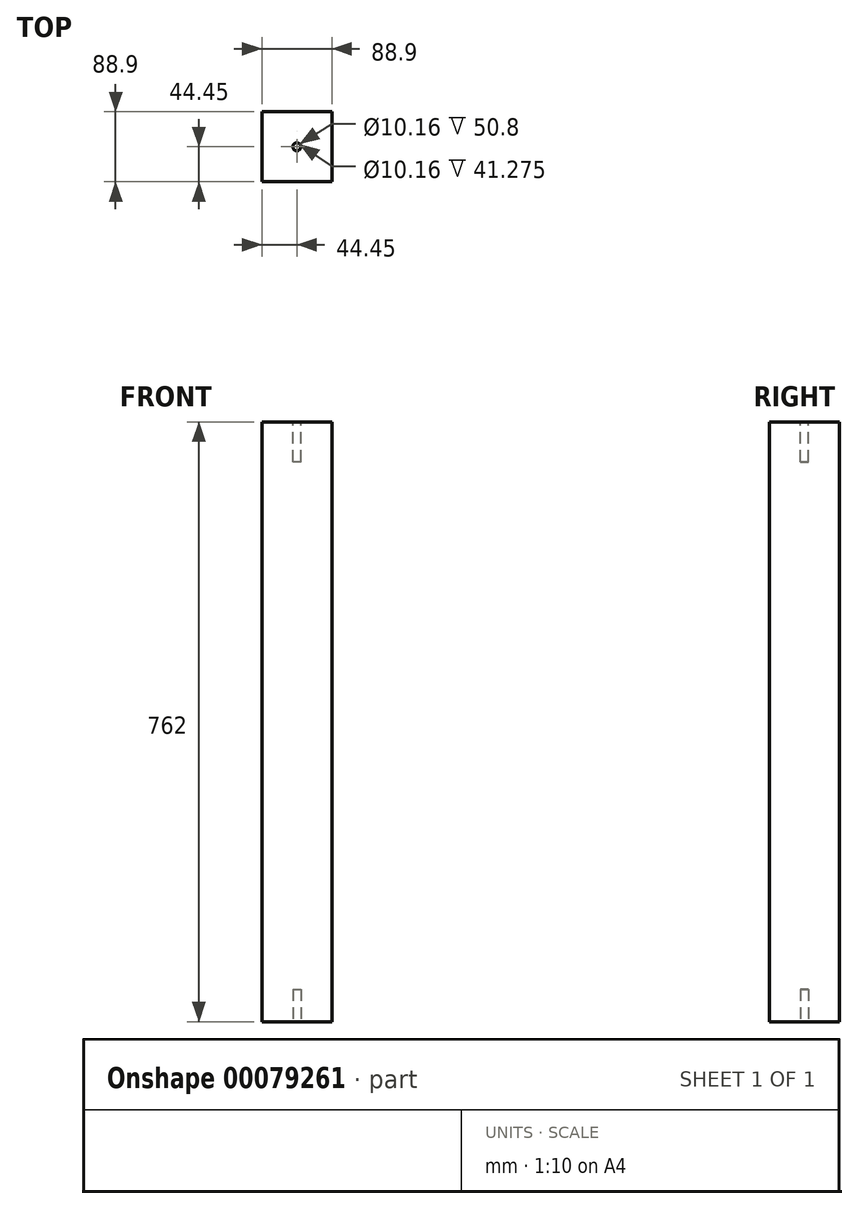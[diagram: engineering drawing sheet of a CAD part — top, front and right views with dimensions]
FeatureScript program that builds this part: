
annotation { "Feature Type Name" : "Feature", "Feature Type Description" : "" }
export const myFeature = defineFeature(function(context is Context, id is Id, definition is map)
    precondition{}
    {
        {
            var Q0;
            Q0=qCreatedBy(makeId("Top.planeOp"),FACE);
            var sketch = newSketch(context, id + "F0", { "sketchPlane" : qUnion([Q0])});
            skLineSegment(sketch, "E0.bottom", {"start": v(0, 0) * mm, "end": v(-88.9, 0) * mm});
            skLineSegment(sketch, "E0.top", {"start": v(0, 88.9) * mm, "end": v(-88.9, 88.9) * mm});
            skLineSegment(sketch, "E0.left", {"start": v(0, 0) * mm, "end": v(0, 88.9) * mm});
            skLineSegment(sketch, "E0.right", {"start": v(-88.9, 0) * mm, "end": v(-88.9, 88.9) * mm});
            skSolve(sketch);
        }
        {
            var Q0;
            Q0=makeQuery(id+"F0.imprint","IMPRINT",FACE,{"disambiguationData":[TD([[makeQuery(id+"F0.imprint","IMPRINT",EDGE,{"derivedFrom":sQuery(id+"F0.wireOp",EDGE,"E0.bottom")}),-1.0]])]});
            extrude(context, id + "F1", {"entities" : qUnion([Q0]), "depth" : 762 * mm});
        }
        {
            var Q0;
            Q0=makeQuery(id+"F1.opExtrude","CAP_FACE",FACE,{"disambiguationData":[OSD([sQuery(id+"F0.wireOp",EDGE,"E0.bottom"),sQuery(id+"F0.wireOp",EDGE,"E0.top"),sQuery(id+"F0.wireOp",EDGE,"E0.left"),sQuery(id+"F0.wireOp",EDGE,"E0.right")])],"isStart":false});
            var sketch = newSketch(context, id + "F2", { "sketchPlane" : qUnion([Q0])});
            skCircle(sketch, "E1", {"center": v(-44.45, 44.45) * mm, "radius": 5.08 * mm});
            skPoint(sketch, "E1.centerSnap0", {"position": v(-44.45, 0) * mm});
            skSolve(sketch);
        }
        {
            var Q0;
            Q0=makeQuery(id+"F2.imprint","IMPRINT",FACE,{"disambiguationData":[TD([[makeQuery(id+"F2.imprint","IMPRINT",EDGE,{"derivedFrom":sQuery(id+"F2.wireOp",EDGE,"E1")}),1.0]])]});
            extrude(context, id + "F3", {"entities" : qUnion([Q0]), "operationType" : NewBodyOperationType.REMOVE, "oppositeDirection" : true, "depth" : 50.8 * mm});
        }
        {
            var Q0;
            Q0=makeQuery(id+"F1.opExtrude","CAP_FACE",FACE,{"disambiguationData":[OSD([sQuery(id+"F0.wireOp",EDGE,"E0.bottom"),sQuery(id+"F0.wireOp",EDGE,"E0.top"),sQuery(id+"F0.wireOp",EDGE,"E0.left"),sQuery(id+"F0.wireOp",EDGE,"E0.right")])],"isStart":true});
            var sketch = newSketch(context, id + "F4", { "sketchPlane" : qUnion([Q0])});
            skCircle(sketch, "E2", {"center": v(-44.45, -44.45) * mm, "radius": 5.08 * mm});
            skPoint(sketch, "E2.centerSnap0", {"position": v(-44.45, -88.9) * mm});
            skSolve(sketch);
        }
        {
            var Q0;
            Q0=makeQuery(id+"F4.imprint","IMPRINT",FACE,{"disambiguationData":[TD([[makeQuery(id+"F4.imprint","IMPRINT",EDGE,{"derivedFrom":sQuery(id+"F4.wireOp",EDGE,"E2")}),1.0]])]});
            extrude(context, id + "F5", {"entities" : qUnion([Q0]), "operationType" : NewBodyOperationType.REMOVE, "oppositeDirection" : true, "depth" : 41.27 * mm});
        }
    });
